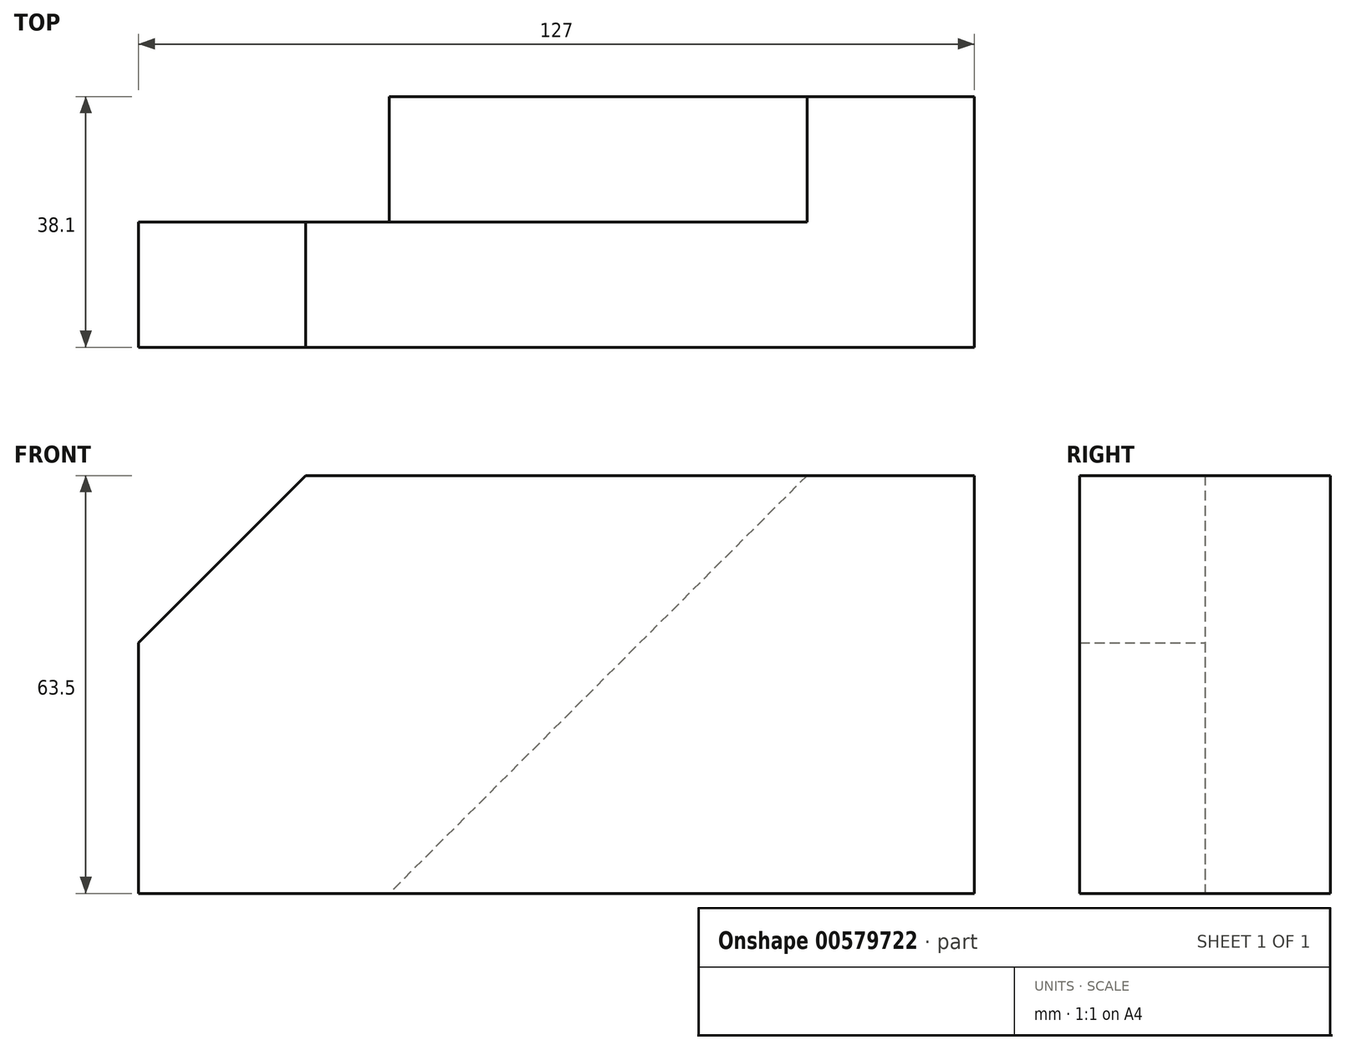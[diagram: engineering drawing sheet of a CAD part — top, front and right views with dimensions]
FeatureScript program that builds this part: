
annotation { "Feature Type Name" : "Feature", "Feature Type Description" : "" }
export const myFeature = defineFeature(function(context is Context, id is Id, definition is map)
    precondition{}
    {
        {
            var Q0;
            Q0=qCreatedBy(makeId("Front.planeOp"),FACE);
            var sketch = newSketch(context, id + "F0", { "sketchPlane" : qUnion([Q0])});
            skLineSegment(sketch, "E0.bottom", {"start": v(-57.85, 12.56) * mm, "end": v(69.15, 12.56) * mm});
            skLineSegment(sketch, "E0.top", {"start": v(-57.85, -50.94) * mm, "end": v(69.15, -50.94) * mm});
            skLineSegment(sketch, "E0.left", {"start": v(-57.85, 12.56) * mm, "end": v(-57.85, -50.94) * mm});
            skLineSegment(sketch, "E0.right", {"start": v(69.15, 12.56) * mm, "end": v(69.15, -50.94) * mm});
            skSolve(sketch);
        }
        {
            var Q0;
            Q0=makeQuery(id+"F0.imprint","IMPRINT",FACE,{"disambiguationData":[TD([[makeQuery(id+"F0.imprint","IMPRINT",EDGE,{"derivedFrom":sQuery(id+"F0.wireOp",EDGE,"E0.bottom")}),-1.0]])]});
            extrude(context, id + "F1", {"entities" : qUnion([Q0]), "depth" : 38.1 * mm, "offsetDistance" : 25.4 * mm});
        }
        {
            var Q0;
            Q0=qCreatedBy(makeId("Front.planeOp"),FACE);
            var sketch = newSketch(context, id + "F2", { "sketchPlane" : qUnion([Q0])});
            skLineSegment(sketch, "E1", {"start": v(-32.45, 12.56) * mm, "end": v(-57.85, -12.84) * mm});
            skLineSegment(sketch, "E2", {"start": v(-32.45, 12.56) * mm, "end": v(-62, 12.56) * mm});
            skLineSegment(sketch, "E3", {"start": v(-62, 12.56) * mm, "end": v(-62, -12.83) * mm});
            skLineSegment(sketch, "E4", {"start": v(-62, -12.83) * mm, "end": v(-57.85, -12.84) * mm});
            skSolve(sketch);
        }
        {
            var Q0;
            Q0=makeQuery(id+"F2.imprint","IMPRINT",FACE,{"disambiguationData":[TD([[makeQuery(id+"F2.imprint","IMPRINT",EDGE,{"derivedFrom":sQuery(id+"F2.wireOp",EDGE,"E1")}),-1.0]])]});
            extrude(context, id + "F3", {"entities" : qUnion([Q0]), "operationType" : NewBodyOperationType.REMOVE, "depth" : 50.8 * mm, "offsetDistance" : 25.4 * mm});
        }
        {
            var Q0;
            Q0=qCreatedBy(makeId("Front.planeOp"),FACE);
            var sketch = newSketch(context, id + "F4", { "sketchPlane" : qUnion([Q0])});
            skLineSegment(sketch, "E5", {"start": v(43.75, 12.56) * mm, "end": v(-19.75, -50.94) * mm});
            skLineSegment(sketch, "E6", {"start": v(43.75, 12.56) * mm, "end": v(-59.24, 12.56) * mm});
            skLineSegment(sketch, "E7", {"start": v(-59.24, 12.56) * mm, "end": v(-59.24, -51) * mm});
            skLineSegment(sketch, "E8", {"start": v(-59.24, -51) * mm, "end": v(-19.75, -50.94) * mm});
            skSolve(sketch);
        }
        {
            var Q0;
            Q0 = qSketchRegion(id + "F4", true);
            extrude(context, id + "F5", {"entities" : qUnion([Q0]), "operationType" : NewBodyOperationType.REMOVE, "depth" : 19.05 * mm, "offsetDistance" : 25.4 * mm});
        }
    });
